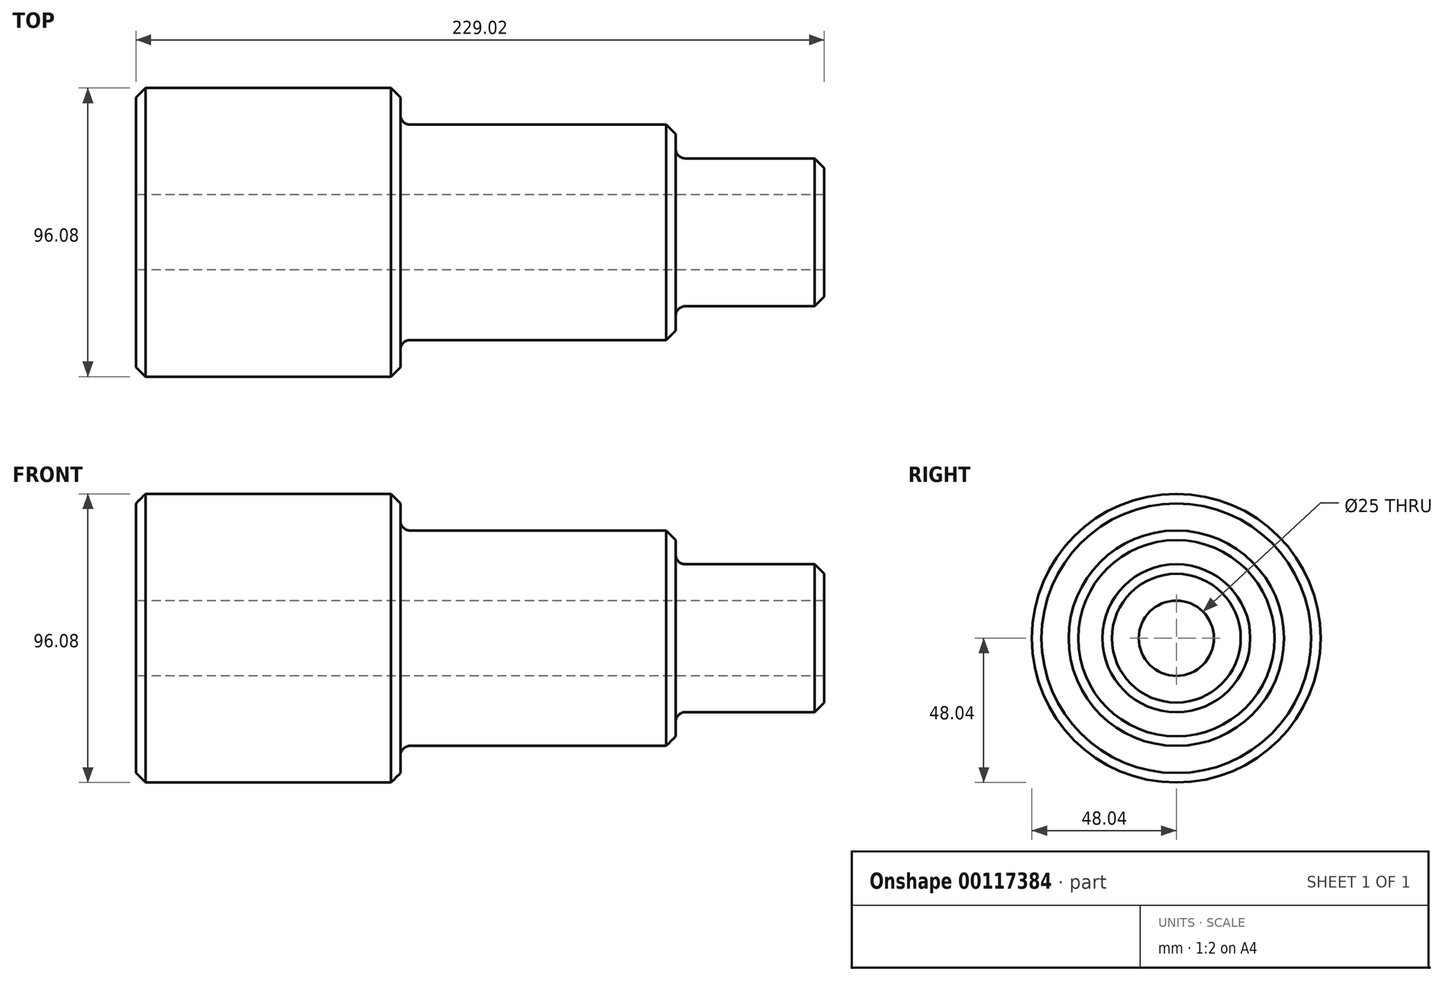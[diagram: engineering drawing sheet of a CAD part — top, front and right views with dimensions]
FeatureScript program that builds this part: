
annotation { "Feature Type Name" : "Feature", "Feature Type Description" : "" }
export const myFeature = defineFeature(function(context is Context, id is Id, definition is map)
    precondition{}
    {
        {
            var Q0;
            Q0=qCreatedBy(makeId("Top.planeOp"),FACE);
            var sketch = newSketch(context, id + "F0", { "sketchPlane" : qUnion([Q0])});
            skLineSegment(sketch, "E0", {"start": v(-118.94, 0) * mm, "end": v(110.08, 0) * mm});
            skLineSegment(sketch, "E1", {"start": v(-118.94, 0) * mm, "end": v(-118.94, 48.04) * mm});
            skLineSegment(sketch, "E2", {"start": v(-118.94, 48.04) * mm, "end": v(-30.91, 48.04) * mm});
            skLineSegment(sketch, "E3", {"start": v(-30.91, 48.04) * mm, "end": v(-30.91, 35.83) * mm});
            skLineSegment(sketch, "E4", {"start": v(-30.91, 35.83) * mm, "end": v(60.66, 35.83) * mm});
            skLineSegment(sketch, "E5", {"start": v(60.66, 35.83) * mm, "end": v(60.66, 24.6) * mm});
            skLineSegment(sketch, "E6", {"start": v(60.66, 24.6) * mm, "end": v(110.08, 24.6) * mm});
            skLineSegment(sketch, "E7", {"start": v(110.08, 24.6) * mm, "end": v(110.08, 0) * mm});
            skSolve(sketch);
        }
        {
            var Q0;
            Q0=makeQuery(id+"F0.imprint","IMPRINT",FACE,{"disambiguationData":[TD([[makeQuery(id+"F0.imprint","IMPRINT",EDGE,{"derivedFrom":sQuery(id+"F0.wireOp",EDGE,"E0")}),1.0]])]});
            var Q1;
            Q1=sQuery(id+"F0.wireOp",EDGE,"E0");
            revolve(context, id + "F1", {"entities" : qUnion([Q0]), "axis" : qUnion([Q1]), "revolveType" : RevolveType.FULL});
        }
        {
            var Q0;
            Q0=makeQuery(id+"F1.opRevolve","SWEPT_FACE",FACE,{"disambiguationData":[OSD([sQuery(id+"F0.wireOp",EDGE,"E1")])]});
            var sketch = newSketch(context, id + "F2", { "sketchPlane" : qUnion([Q0])});
            skCircle(sketch, "E8", {"center": v(0, 0) * mm, "radius": 12.5 * mm});
            skSolve(sketch);
        }
        {
            var Q0;
            Q0=makeQuery(id+"F2.imprint","IMPRINT",FACE,{"disambiguationData":[TD([[makeQuery(id+"F2.imprint","IMPRINT",EDGE,{"derivedFrom":sQuery(id+"F2.wireOp",EDGE,"E8")}),1.0]])]});
            extrude(context, id + "F3", {"entities" : qUnion([Q0]), "operationType" : NewBodyOperationType.REMOVE, "oppositeDirection" : true, "depth" : 253.15 * mm});
        }
        {
            var Q0;
            Q0=makeQuery(id+"F1.opRevolve","SWEPT_EDGE",EDGE,{"disambiguationData":[OSD([sQuery(id+"F0.wireOp",EDGE,"E1"),sQuery(id+"F0.wireOp",EDGE,"E2")])]});
            var Q1;
            Q1=makeQuery(id+"F1.opRevolve","SWEPT_EDGE",EDGE,{"disambiguationData":[OSD([sQuery(id+"F0.wireOp",EDGE,"E2"),sQuery(id+"F0.wireOp",EDGE,"E3")])]});
            var Q2;
            Q2=makeQuery(id+"F1.opRevolve","SWEPT_EDGE",EDGE,{"disambiguationData":[OSD([sQuery(id+"F0.wireOp",EDGE,"E4"),sQuery(id+"F0.wireOp",EDGE,"E5")])]});
            var Q3;
            Q3=makeQuery(id+"F1.opRevolve","SWEPT_EDGE",EDGE,{"disambiguationData":[OSD([sQuery(id+"F0.wireOp",EDGE,"E6"),sQuery(id+"F0.wireOp",EDGE,"E7")])]});
            chamfer(context, id + "F4", {"entities" : qUnion([Q0, Q1, Q2, Q3]), "width" : 3.17 * mm, "tangentPropagation" : true});
        }
        {
            var Q0;
            Q0=makeQuery(id+"F1.opRevolve","SWEPT_EDGE",EDGE,{"disambiguationData":[OSD([sQuery(id+"F0.wireOp",EDGE,"E5"),sQuery(id+"F0.wireOp",EDGE,"E6")])]});
            var Q1;
            Q1=makeQuery(id+"F1.opRevolve","SWEPT_EDGE",EDGE,{"disambiguationData":[OSD([sQuery(id+"F0.wireOp",EDGE,"E3"),sQuery(id+"F0.wireOp",EDGE,"E4")])]});
            fillet(context, id + "F5", {"entities" : qUnion([Q0, Q1]), "radius" : 3.17 * mm, "tangentPropagation" : true, "allowEdgeOverflow" : false});
        }
    });
